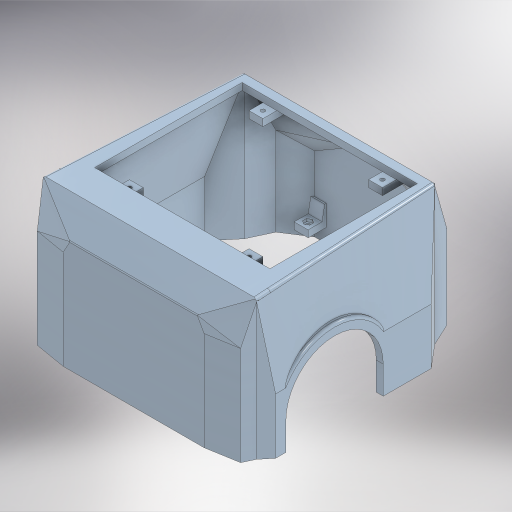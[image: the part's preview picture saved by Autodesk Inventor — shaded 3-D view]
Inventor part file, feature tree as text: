
AUTODESK INVENTOR PART (.ipt)
format: ipt  version: 2024 (Build 280153000, 153)  size: 1,922,560 bytes
history: native  units: mm
features: other x52, sketch x36, extrude x34, loft x18, fillet x7, plane x1
ambient origin geometry x8: Origin, YZ Plane, XZ Plane, XY Plane, X Axis, Y Axis, Z Axis, Center Point
bodies: Body1 (feature_tree), Body2 (feature_tree)
feature tree (148):
  other  "Sólido1"
  extrude  "Base"  Depth=10.0mm TaperAngle=0.0deg
  extrude  "Llantas"  Depth=70.0mm
  extrude  "Carroceria"  Depth=75.0mm
  extrude  "Extrusión30"  Depth=150.0mm
  extrude  "Extrusión31"  Depth=10.0mm TaperAngle=0.0deg
  extrude  "Extrusión32"  Depth=8.726646mm
  extrude  "Extrusión33"  Depth=40.0mm
  extrude  "Extrusión34"  Depth=15.0mm
  extrude  "Extrusión35"  Depth=50.0mm
  extrude  "Extrusión38"  Depth=11.34464mm
  extrude  "Extrusión39"  Depth=5.0mm
  extrude  "Extrusión100"  Depth=10.0mm
  extrude  "Extrusión102"  Depth=5.0mm
  extrude  "Extrusión103"  Depth=5.0mm
  extrude  "Extrusión104"  TaperAngle=0.0deg  [1 undecoded]
  loft  "Solevación32"
  loft  "Solevación33"
  extrude  "Extrusión43"  TaperAngle=0.0deg  [1 undecoded]
  extrude  "Extrusión96"  Depth=3.0mm
  extrude  "Extrusión110"  Depth=3.0mm
  extrude  "Extrusión90"  Depth=3.0mm
  extrude  "Extrusión94"  Depth=3.0mm
  extrude  "Extrusión95"  Depth=5.0mm
  loft  "Solevación10"
  loft  "Solevación11"
  extrude  "Extrusión53"  TaperAngle=0.0deg  [1 undecoded]
  extrude  "Extrusión93"  TaperAngle=0.0deg  [1 undecoded]
  loft  "Solevación8"
  loft  "Solevación9"
  extrude  "Extrusión84"  Depth=80.0mm TaperAngle=0.0deg
  extrude  "Extrusión64"  Depth=5.0mm
  extrude  "Extrusión65"  Depth=5.0mm TaperAngle=0.0deg
  extrude  "Extrusión67"  Depth=5.0mm TaperAngle=0.0deg
  extrude  "Extrusión111"  Depth=6.0mm
  plane  "Plano de trabajo5"
  extrude  "Extrusión98"  Depth=3.0mm
  loft  "Solevación18"
  loft  "Solevación19"
  loft  "Solevación20"
  loft  "Solevación21"
  loft  "Solevación22"
  loft  "Solevación23"
  loft  "Solevación24"
  loft  "Solevación30"
  loft  "Solevación26"
  loft  "Solevación31"
  loft  "Solevación34"
  loft  "Solevación35"
  fillet  "Empalme1"  Radius=15.0mm
  fillet  "Empalme2"  Radius=10.0mm
  fillet  "Empalme3"  Radius=5.0mm
  fillet  "Empalme4"  Radius=85.592mm
  fillet  "Empalme5"  Radius=10.0mm
  fillet  "Empalme6"  Radius=10.0mm
  fillet  "Empalme7"  Radius=100.0mm
  extrude  "Extrusión105"  TaperAngle=30.0deg  [1 undecoded]
  extrude  "Extrusión106"  Depth=10.0mm
  extrude  "Extrusión107"  Depth=10.0mm TaperAngle=0.0deg
  extrude  "Extrusión108"  Depth=10.0mm
  extrude  "Extrusión109"  Depth=10.0mm TaperAngle=0.0deg
  sketch  "Boceto Base"  dims[d346=5.0mm d347=0.0mm d348=6.0mm]
  sketch  "Boceto Llantas"  dims[d349=70.0mm d350=0.0mm d368=3.0mm]
  sketch  "Boceto Carroceria"  dims[d369=5.0mm d370=47.5mm d371=5.0mm d372=5.0mm d373=5.0mm d374=15.0mm d375=0.0mm d396=70.0mm d397=0.0mm d422=3.0mm d424=37.5mm d425=5.0mm d426=5.0mm d427=5.0mm d428=5.0mm d429=15.0mm d430=0.0mm d431=10.0mm d432=5.0mm d433=85.592mm d434=0.0mm d439=10.0mm d440=0.0mm d494=10.0mm d495=0.0mm d514=100.0mm d515=0.0mm d530=30.0deg d531=30.0mm d532=10.0mm d533=0.0mm d534=0.0mm d535=90.0deg d536=0.0mm d537=90.0deg d538=0.0mm d539=90.0deg d540=0.0mm d541=90.0deg d542=11.34464mm d543=10.0mm d544=0.0mm d545=11.34464mm d546=0.0mm d547=10.0mm d548=0.0mm d549=5.0mm d550=10.0mm d551=105.0mm d552=0.0mm d553=0.0mm d554=90.0deg d559=0.0mm d560=90.0deg d595=20.0mm d596=20.0mm d597=30.0mm d598=30.0mm d599=5.0mm d600=0.0mm d611=5.0mm d612=0.0mm d613=90.0deg d614=0.0mm d615=90.0deg d616=0.0mm d617=90.0deg d618=0.0mm d619=90.0deg d620=0.0mm d621=90.0deg d622=0.0mm d623=90.0deg d624=0.0mm d625=90.0deg d626=0.0mm d627=90.0deg d628=0.0mm d629=90.0deg d630=0.0mm d631=90.0deg d632=5.0mm d633=0.0mm d634=90.0deg d635=0.0mm d636=90.0deg d637=0.0mm d638=90.0deg d639=0.0mm d640=90.0deg d645=0.0mm d646=90.0deg d647=0.0mm d648=90.0deg d653=20.0mm d654=85.0mm d655=42.5mm d656=70.0mm d657=200.0mm d658=0.0mm d669=40.0mm d670=0.0mm d671=0.0mm d672=90.0deg d673=0.0mm d674=90.0deg d676=0.0mm d677=90.0deg d680=0.0mm d681=90.0deg d684=5.0mm d685=0.0mm d686=5.0mm d687=0.0mm d688=0.0mm d689=90.0deg d690=0.0mm d691=90.0deg d692=0.0mm d693=90.0deg d694=0.0mm d695=90.0deg d697=0.0mm d698=90.0deg d699=0.0mm d700=90.0deg d701=0.0mm d702=90.0deg d703=0.0mm d704=90.0deg d705=2.0mm d706=2.0mm d707=2.0mm d708=2.0mm d709=2.0mm d710=2.0mm d711=2.0mm d712=100.0mm d713=0.0mm d714=100.0mm d715=0.0mm d716=10.0mm d717=15.0mm d718=10.0mm d719=10.0mm d720=15.0mm d723=10.0mm d724=10.0mm d725=3.0mm d726=5.0mm d727=5.0mm d728=3.0mm d729=5.0mm d730=5.0mm d731=5.0mm d732=0.0mm d733=5.0mm d734=10.0mm d735=0.0mm d737=5.0mm d738=10.0mm d739=0.0mm d740=3.0mm d741=120.0deg d742=120.0deg d743=3.0mm d744=120.0deg d745=3.0mm d746=120.0deg d747=2.598mm d748=5.196152mm d749=3.0mm d750=2.0mm d751=0.0mm d752=3.0mm d753=3.0mm d754=120.0deg d755=3.0mm d756=120.0deg d757=3.0mm d758=3.0mm d759=120.0deg d760=3.0mm d761=2.598mm d762=2.0mm d763=0.0mm d764=0.0mm d765=90.0deg d766=0.0mm d767=90.0deg d64=0.5mm d65=0.872665mm d66=0.5mm d67=0.872665mm d229=0.5mm d230=0.872665mm d231=0.5mm d232=0.872665mm d284=0.5mm d285=0.872665mm d286=0.5mm d287=0.872665mm d288=0.5mm d289=0.872665mm d290=0.5mm d342=0.5mm d343=0.872665mm d344=0.5mm d345=0.872665mm d352=0.5mm d353=0.872665mm d354=0.5mm d355=0.872665mm d364=0.5mm d365=0.872665mm d366=0.5mm d367=0.872665mm d386=0.5mm d387=0.872665mm d388=0.5mm d389=0.872665mm d472=0.5mm d473=0.872665mm d474=0.5mm d475=0.872665mm d525=0.5mm d526=0.872665mm d527=0.5mm d528=0.872665mm]
  sketch  "Boceto28"  dims[d0=160.0mm d2=10.0mm d3=0.0mm]
  sketch  "Boceto30"  dims[d4=70.0mm d5=70.0mm]
  sketch  "Boceto31"  dims[d6=20.0mm d7=75.0mm]
  sketch  "Boceto32"  dims[d8=80.0mm d9=150.0mm]
  sketch  "Boceto33"  dims[d10=25.0mm d11=10.0mm d12=0.0mm]
  sketch  "Boceto34"  dims[d13=30.0mm d14=8.726646mm]
  sketch  "Boceto37"  dims[d15=11.34464mm d16=40.0mm]
  sketch  "Boceto38"  dims[d17=15.0mm d18=15.0mm]
  sketch  "Boceto43"  dims[d19=6.0mm d20=50.0mm]
  sketch  "Boceto54"  dims[d21=8.726646mm d22=11.34464mm]
  sketch  "Boceto64"  dims[d23=6.0mm d24=5.0mm]
  sketch  "Boceto65"  dims[d25=10.0mm d26=0.0mm d291=3.0mm]
  sketch  "Boceto67"  dims[d292=5.0mm d293=5.0mm]
  sketch  "Boceto106"  dims[d294=3.0mm d295=5.0mm]
  sketch  "Boceto114"  dims[d297=3.0mm d298=0.0mm]
  sketch  "Boceto117"  dims[d299=0.0mm d300=0.0mm]
  sketch  "Boceto118"  dims[d301=0.0mm d303=5.0mm]
  sketch  "Boceto119"  dims[d304=3.0mm d305=0.0mm]
  sketch  "Boceto120"  dims[d306=5.0mm d307=3.0mm]
  sketch  "Boceto125"  dims[d308=5.0mm d309=3.0mm]
  sketch  "Boceto129"  dims[d310=5.0mm d311=3.0mm]
  other  "Aristas31"
  other  "Aristas32"
  other  "Aristas33"
  other  "Aristas34"
  other  "Aristas35"
  other  "Aristas36"
  other  "Aristas37"
  other  "Aristas38"
  other  "Aristas39"
  sketch  "Boceto131"  dims[d312=5.0mm d313=3.0mm]
  other  "Aristas40"
  other  "Aristas47"
  other  "Aristas48"
  other  "Sólido8"
  other  "Aristas49"
  other  "Aristas50"
  sketch  "Boceto132"  dims[d314=3.0mm d315=5.0mm]
  sketch  "Boceto135"  dims[d316=0.0mm d317=0.0mm]
  other  "Aristas57"
  other  "Aristas58"
  other  "Aristas59"
  other  "Aristas60"
  sketch  "Boceto138"  dims[d318=0.0mm d319=0.0mm]
  sketch  "Boceto139"  dims[d320=0.0mm d321=0.0mm]
  other  "Aristas65"
  other  "Aristas66"
  other  "Aristas67"
  other  "Aristas68"
  other  "Aristas69"
  other  "Aristas70"
  other  "Aristas71"
  other  "Aristas72"
  sketch  "Boceto142"  dims[d322=0.0mm d323=0.0mm]
  sketch  "Boceto143"  dims[d324=0.0mm d325=0.0mm]
  sketch  "Boceto144"  dims[d326=0.0mm d327=0.1mm d328=0.0mm]
  sketch  "Boceto145"  dims[d329=0.0mm d330=80.0mm d331=0.0mm]
  sketch  "Boceto146"  dims[d332=71.0mm d333=0.0mm d334=5.0mm]
  sketch  "Boceto148"  dims[d335=5.0mm d336=5.0mm d337=0.0mm]
  other  "Aristas73"
  other  "Aristas74"
  other  "Aristas75"
  other  "Aristas76"
  sketch  "Boceto149"  dims[d338=100.0mm d339=0.0mm d340=5.0mm d341=0.0mm]
  other  "Aristas77"
  other  "Aristas78"
  other  "Aristas79"
  other  "Aristas80"
  other  "Finish1"
  other  "Finish2"
  other  "Finish3"
  other  "Finish4"
  other  "Finish5"
  other  "Finish6"
  other  "Finish7"
  other  "Finish8"
  other  "Finish9"
  other  "Finish10"
  other  "Finish11"
  other  "Finish12"
  other  "Finish13"
  other  "Finish14"
  other  "Finish15"
  other  "Finish16"
note: 5 required parameter values undecoded (feature->parameter linkage not recoverable at this tier; creation-order binding heuristic only, values carry confidence <= 0.55)
